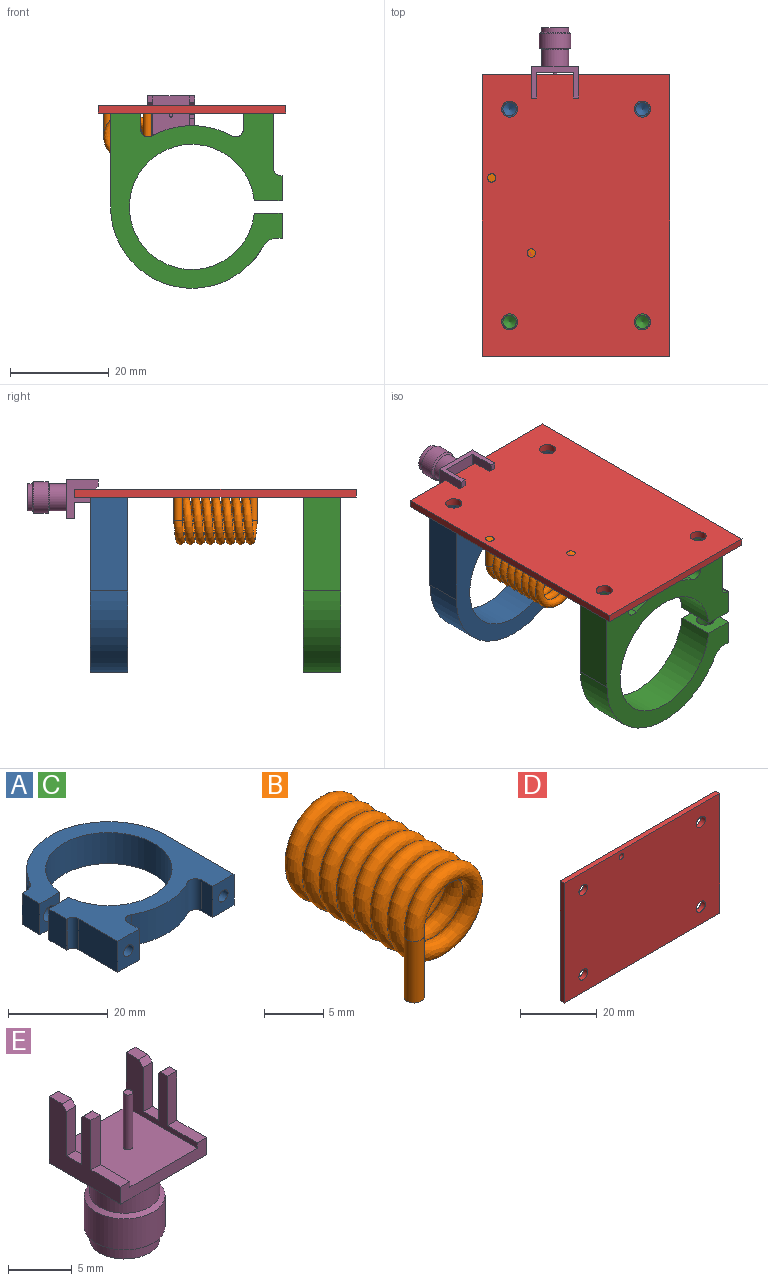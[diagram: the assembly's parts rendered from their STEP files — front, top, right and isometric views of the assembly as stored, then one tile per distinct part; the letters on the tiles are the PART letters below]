
ASSEMBLY  parts=5 mates=4
PART A: 32 faces, bbox 34.8x35.6x7.6 mm
  f0: cylinder r=1.35mm len=5.08mm, axis (0,1,0), area 43.2mm2, adj f1,f27
  f1: cone r=1.35mm half-angle=59deg, axis (0,1,0), area 6.7mm2, adj f0
  f2: cylinder r=1.78mm len=5.08mm, axis (0,1,0), area 56.8mm2, adj f11,f25
  f3: cylinder r=3.11mm len=6.22mm, axis (0,-1,0), area 29.7mm2, adj f10,f11,f12,f13,f30,f31
  f4: cylinder r=1.35mm len=7.62mm, axis (0,-1,0), area 64.8mm2, adj f5,f14
  f5: cone r=1.35mm half-angle=59deg, axis (0,-1,0), area 6.7mm2, adj f4
  f6: cylinder r=1.35mm len=7.62mm, axis (0,-1,0), area 64.8mm2, adj f7,f16
  f7: cone r=1.35mm half-angle=59deg, axis (0,-1,0), area 6.7mm2, adj f6
  f8: cylinder r=16.51mm len=16.14mm, axis (0,0,1), area 128.5mm2, adj f18,f19,f22,f23
  f9: cylinder r=12.7mm len=25.4mm, axis (0,0,1), area 588.7mm2, adj f18,f19,f25,f27
  f10: cylinder r=16.51mm len=30.96mm, axis (0,0,-1), area 316.2mm2, adj f3,f12,f13,f17,f18,f19
  f11: plane 7.62x5.88mm, normal (0,1,0), area 24mm2, adj f2,f3,f12,f13,f18,f19,f24,f30
  f12: cylinder r=3.17mm len=2.78mm, axis (0,0,-1), area 2.5mm2, adj f3,f10,f11,f19,f30
  f13: cylinder r=3.17mm len=2.78mm, axis (0,0,-1), area 2.5mm2, adj f3,f10,f11,f18,f31
  f14: plane 7.62x6.08mm, normal (0,-1,0), area 40.6mm2, adj f4,f15,f18,f19,f20
  f15: plane 11.18x7.62mm, normal (-1,0,0), area 85.2mm2, adj f14,f18,f19,f29
  f16: plane 7.62x6.08mm, normal (0,-1,0), area 40.6mm2, adj f6,f17,f18,f19,f21
  f17: plane 19.05x7.62mm, normal (1,0,0), area 145.2mm2, adj f10,f16,f18,f19
  f18: plane 35.56x34.8mm, normal (0,0,1), area 488.9mm2, adj f8,f9,f10,f11,f13,f14,f15,f16
  f19: plane 35.56x34.8mm, normal (0,0,-1), area 488.9mm2, adj f8,f9,f10,f11,f12,f14,f15,f16
  f20: plane 7.62x3.26mm, normal (1,0,0), area 24.9mm2, adj f14,f18,f19,f23
  f21: plane 7.62x3.26mm, normal (-1,0,0), area 24.9mm2, adj f16,f18,f19,f22
  f22: cylinder r=1.58mm len=7.62mm, axis (0,0,1), area 25.1mm2, adj f8,f18,f19,f21
  f23: cylinder r=1.58mm len=7.62mm, axis (0,0,1), area 25.1mm2, adj f8,f18,f19,f20
  f24: plane 7.62x5.08mm, normal (-1,0,0), area 38.7mm2, adj f11,f18,f19,f25
  f25: plane 7.62x5.65mm, normal (0,-1,0), area 33.1mm2, adj f2,f9,f18,f19,f24
  f26: plane 7.62x5.08mm, normal (-1,0,0), area 38.7mm2, adj f18,f19,f27,f28
  f27: plane 7.62x5.65mm, normal (0,1,0), area 37.3mm2, adj f0,f9,f18,f19,f26
  f28: plane 7.62x0.25mm, normal (0,-1,0), area 1.9mm2, adj f18,f19,f26,f29
  f29: cylinder r=1.52mm len=7.62mm, axis (0,0,1), area 18.2mm2, adj f15,f18,f19,f28
  f30: plane 1.71x0.5mm, normal (0,0,1), area 0.3mm2, adj f3,f11,f12
  f31: plane 1.71x0.5mm, normal (0,0,-1), area 0.3mm2, adj f3,f11,f13
PART B: 5 faces, bbox 9.8x19x12 mm
  f0: bspline ~18.98x11.26mm, area 1019.4mm2, adj f1,f3
  f1: cylinder r=0.85mm len=6.35mm, axis (0,0,1), area 33.9mm2, adj f0,f2
  f2: plane 1.7x1.7mm, normal (0,0,-1), area 2.3mm2, adj f1
  f3: cylinder r=0.85mm len=6.35mm, axis (0,0,1), area 33.9mm2, adj f0,f4
  f4: plane 1.7x1.7mm, normal (0,0,-1), area 2.3mm2, adj f3
PART C: same geometry as A
PART D: 11 faces, bbox 57.2x1.5x38.1 mm
  f0: plane 38.1x1.55mm, normal (1,0,0), area 59mm2, adj f1,f3,f4,f5
  f1: plane 57.15x1.55mm, normal (0,0,1), area 88.5mm2, adj f0,f2,f4,f5
  f2: plane 38.1x1.55mm, normal (-1,0,0), area 59mm2, adj f1,f3,f4,f5
  f3: plane 57.15x1.55mm, normal (0,0,-1), area 88.5mm2, adj f0,f2,f4,f5
  f4: plane 57.15x38.1mm, normal (0,-1,0), area 2141.7mm2, adj f0,f1,f2,f3,f6,f7,f8,f9
  f5: plane 57.15x38.1mm, normal (0,1,0), area 2141.7mm2, adj f0,f1,f2,f3,f6,f7,f8,f9
  f6: cylinder r=1.63mm len=3.26mm, axis (0,1,0), area 15.9mm2, adj f4,f5
  f7: cylinder r=1.63mm len=3.26mm, axis (0,1,0), area 15.9mm2, adj f4,f5
  f8: cylinder r=1.63mm len=3.26mm, axis (0,1,0), area 15.9mm2, adj f4,f5
  f9: cylinder r=1.63mm len=3.26mm, axis (0,1,0), area 15.9mm2, adj f4,f5
  f10: cylinder r=0.85mm len=1.7mm, axis (0,1,0), area 8.3mm2, adj f4,f5
PART E: 36 faces, bbox 9.5x7.9x14.3 mm
  f0: cylinder r=2.75mm len=5.5mm, axis (0,0,-1), area 59.9mm2, adj f1,f2
  f1: cone r=2.75mm half-angle=60deg, axis (0,0,-1), area 9.1mm2, adj f0,f3
  f2: plane 9.53x7.93mm, normal (0,0,-1), area 51.8mm2, adj f0,f4,f5,f6,f7
  f3: cylinder r=3.17mm len=6.35mm, axis (0,0,-1), area 59.6mm2, adj f1,f8
  f4: plane 9.53x1.65mm, normal (0,-1,0), area 11.9mm2, adj f2,f5,f6,f9,f10,f11,f12,f13
  f5: plane 7.93x6.4mm, normal (-1,0,0), area 26.9mm2, adj f2,f4,f7,f13,f14,f15,f16,f17
  f6: plane 7.93x6.4mm, normal (1,0,0), area 26.9mm2, adj f2,f4,f7,f9,f22,f23,f24,f25
  f7: plane 9.53x6.4mm, normal (0,1,0), area 21.6mm2, adj f2,f5,f6,f10,f11,f12,f18,f26
  f8: cone r=3.17mm half-angle=60deg, axis (0,0,1), area 9.1mm2, adj f3,f30
  f9: plane 3.32x1.02mm, normal (0,0,1), area 3.4mm2, adj f4,f6,f10,f25
  f10: plane 7.93x5.26mm, normal (-1,0,0), area 17.8mm2, adj f4,f7,f9,f11,f22,f23,f24,f25
  f11: plane 7.93x7.49mm, normal (0,0,1), area 59mm2, adj f4,f7,f10,f12,f31
  f12: plane 7.93x5.26mm, normal (1,0,0), area 17.8mm2, adj f4,f7,f11,f13,f14,f15,f16,f17
  f13: plane 3.32x1.02mm, normal (0,0,1), area 3.4mm2, adj f4,f5,f12,f17
  f14: plane 4.55x1.02mm, normal (0,1,0), area 4.6mm2, adj f5,f12,f15,f21
  f15: plane 1.02x0.2mm, normal (0,0.71,0.71), area 0.3mm2, adj f5,f12,f14,f16
  f16: plane 1.02x0.82mm, normal (0,0,1), area 0.8mm2, adj f5,f12,f15,f17
  f17: plane 4.75x1.02mm, normal (0,-1,0), area 4.8mm2, adj f5,f12,f13,f16
  f18: plane 1.41x1.02mm, normal (0,0,1), area 1.4mm2, adj f5,f7,f12,f19
  f19: plane 1.02x0.5mm, normal (0,-0.71,0.71), area 0.7mm2, adj f5,f12,f18,f20
  f20: plane 4.25x1.02mm, normal (0,-1,0), area 4.3mm2, adj f5,f12,f19,f21
  f21: plane 1.68x1.02mm, normal (0,0,1), area 1.7mm2, adj f5,f12,f14,f20
  f22: plane 4.55x1.02mm, normal (0,1,0), area 4.6mm2, adj f6,f10,f23,f29
  f23: plane 1.02x0.2mm, normal (0,0.71,0.71), area 0.3mm2, adj f6,f10,f22,f24
  f24: plane 1.02x0.82mm, normal (0,0,1), area 0.8mm2, adj f6,f10,f23,f25
  f25: plane 4.75x1.02mm, normal (0,-1,0), area 4.8mm2, adj f6,f9,f10,f24
  f26: plane 1.41x1.02mm, normal (0,0,1), area 1.4mm2, adj f6,f7,f10,f27
  f27: plane 1.02x0.5mm, normal (0,-0.71,0.71), area 0.7mm2, adj f6,f10,f26,f28
  f28: plane 4.25x1.02mm, normal (0,-1,0), area 4.3mm2, adj f6,f10,f27,f29
  f29: plane 1.68x1.02mm, normal (0,0,1), area 1.7mm2, adj f6,f10,f22,f28
  f30: cylinder r=2.75mm len=5.5mm, axis (0,0,-1), area 16.1mm2, adj f8,f32
  f31: cylinder r=0.38mm len=5.26mm, axis (0,0,-1), area 12.4mm2, adj f11,f33
  f32: plane 5.5x5.5mm, normal (0,0,-1), area 7.8mm2, adj f30,f34
  f33: plane 0.75x0.75mm, normal (0,0,1), area 0.4mm2, adj f31
  f34: cylinder r=2.25mm len=7.88mm, axis (0,0,1), area 111.6mm2, adj f32,f35
  f35: plane 4.51x4.51mm, normal (0,0,-1), area 15.9mm2, adj f34
PLACE A rot(axis=(0,0.71,-0.71),180deg) t=(24.31,25.88,20.55)mm
PLACE B rot(axis=(-1,0,0),180deg) t=(11.24,-7.14,34.8)mm
PLACE C rot(axis=(0,0.71,-0.71),180deg) t=(24.31,-17.3,20.55)mm
PLACE D rot(axis=(0.58,-0.58,-0.58),120deg) t=(24.32,0.48,41.15)mm
PLACE E rot(axis=(1,0,0),90deg) t=(20.06,29.06,39.53)mm
MATE fastened C.f4 <-> D.f8  axis (0,0,1) through (37.78,-21.11,39.6)mm
MATE fastened D.f2 <-> E.f29  axis (0,1,0) through (24.32,29.06,40.37)mm
MATE fastened B.f3 <-> D.f10  axis (0,0,1) through (7.22,8.1,41.15)mm
MATE fastened A.f4 <-> D.f9  axis (0,0,1) through (37.78,22.07,39.6)mm
